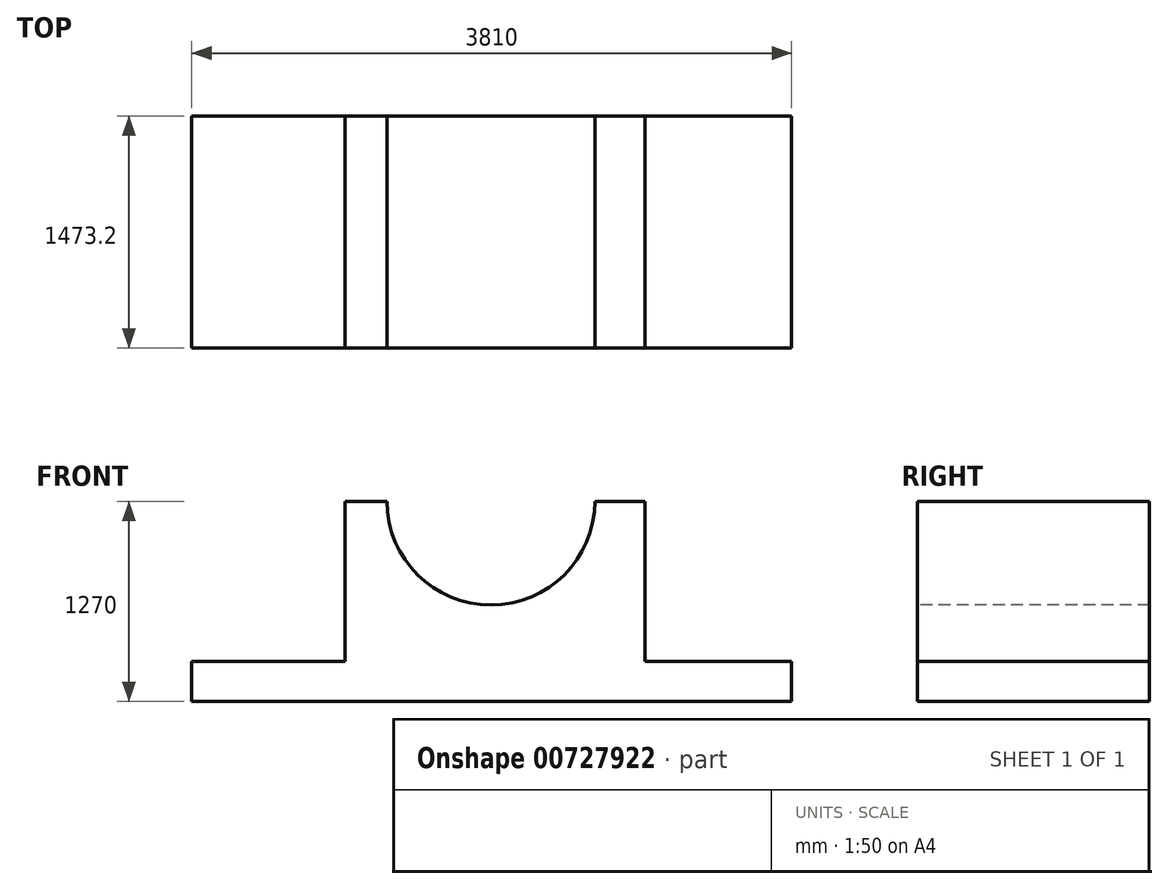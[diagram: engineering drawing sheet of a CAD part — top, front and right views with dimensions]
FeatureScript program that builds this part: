
annotation { "Feature Type Name" : "Feature", "Feature Type Description" : "" }
export const myFeature = defineFeature(function(context is Context, id is Id, definition is map)
    precondition{}
    {
        {
            var Q0;
            Q0=qCreatedBy(makeId("Front.planeOp"),FACE);
            var sketch = newSketch(context, id + "F0", { "sketchPlane" : qUnion([Q0])});
            skLineSegment(sketch, "E0.bottom", {"start": v(-1354.51, -96.43) * mm, "end": v(-381.84, -96.43) * mm});
            skLineSegment(sketch, "E0.top", {"start": v(-1354.51, -350.43) * mm, "end": v(2455.49, -350.43) * mm});
            skLineSegment(sketch, "E0.left", {"start": v(-1354.51, -96.43) * mm, "end": v(-1354.51, -350.43) * mm});
            skLineSegment(sketch, "E0.right", {"start": v(2455.49, -96.43) * mm, "end": v(2455.49, -350.43) * mm});
            skLineSegment(sketch, "E1.top", {"start": v(-381.84, 919.57) * mm, "end": v(1523.16, 919.57) * mm});
            skLineSegment(sketch, "E1.left", {"start": v(-381.84, -96.43) * mm, "end": v(-381.84, 919.57) * mm});
            skLineSegment(sketch, "E1.right", {"start": v(1523.16, -96.43) * mm, "end": v(1523.16, 919.57) * mm});
            skLineSegment(sketch, "E2.trimOffspring", {"start": v(1523.16, -96.43) * mm, "end": v(2455.49, -96.43) * mm});
            skSolve(sketch);
        }
        {
            var Q0;
            Q0=makeQuery(id+"F0.imprint","IMPRINT",FACE,{"disambiguationData":[TD([[makeQuery(id+"F0.imprint","IMPRINT",EDGE,{"derivedFrom":sQuery(id+"F0.wireOp",EDGE,"E0.bottom")}),-1.0]])]});
            extrude(context, id + "F1", {"entities" : qUnion([Q0]), "depth" : 1473.2 * mm, "offsetDistance" : 25.4 * mm});
        }
        {
            var Q0;
            Q0=makeQuery(id+"F1.opExtrude","CAP_FACE",FACE,{"disambiguationData":[OSD([sQuery(id+"F0.wireOp",EDGE,"E0.bottom"),sQuery(id+"F0.wireOp",EDGE,"E0.top"),sQuery(id+"F0.wireOp",EDGE,"E0.left"),sQuery(id+"F0.wireOp",EDGE,"E0.right"),sQuery(id+"F0.wireOp",EDGE,"E1.top"),sQuery(id+"F0.wireOp",EDGE,"E1.left"),sQuery(id+"F0.wireOp",EDGE,"E1.right"),sQuery(id+"F0.wireOp",EDGE,"E2.trimOffspring")])],"isStart":false});
            var sketch = newSketch(context, id + "F2", { "sketchPlane" : qUnion([Q0])});
            skArc(sketch, "E3", {"start": v(-115.13, 919.57) * mm, "mid": v(545.27, 262.2) * mm, "end": v(1205.66, 919.57) * mm});
            skSolve(sketch);
        }
        {
            var Q0;
            {var subQ0=sQuery(id+"F2.wireOp",EDGE,"E3");Q0=makeQuery(id+"F2.imprint","IMPRINT",FACE,{"disambiguationData":[TD([[makeQuery(id+"F2.imprint","IMPRINT",EDGE,{"derivedFrom":subQ0}),1.0]])]});}
            extrude(context, id + "F3", {"entities" : qUnion([Q0]), "operationType" : NewBodyOperationType.REMOVE, "oppositeDirection" : true, "depth" : 1473.2 * mm, "offsetDistance" : 25.4 * mm});
        }
    });
